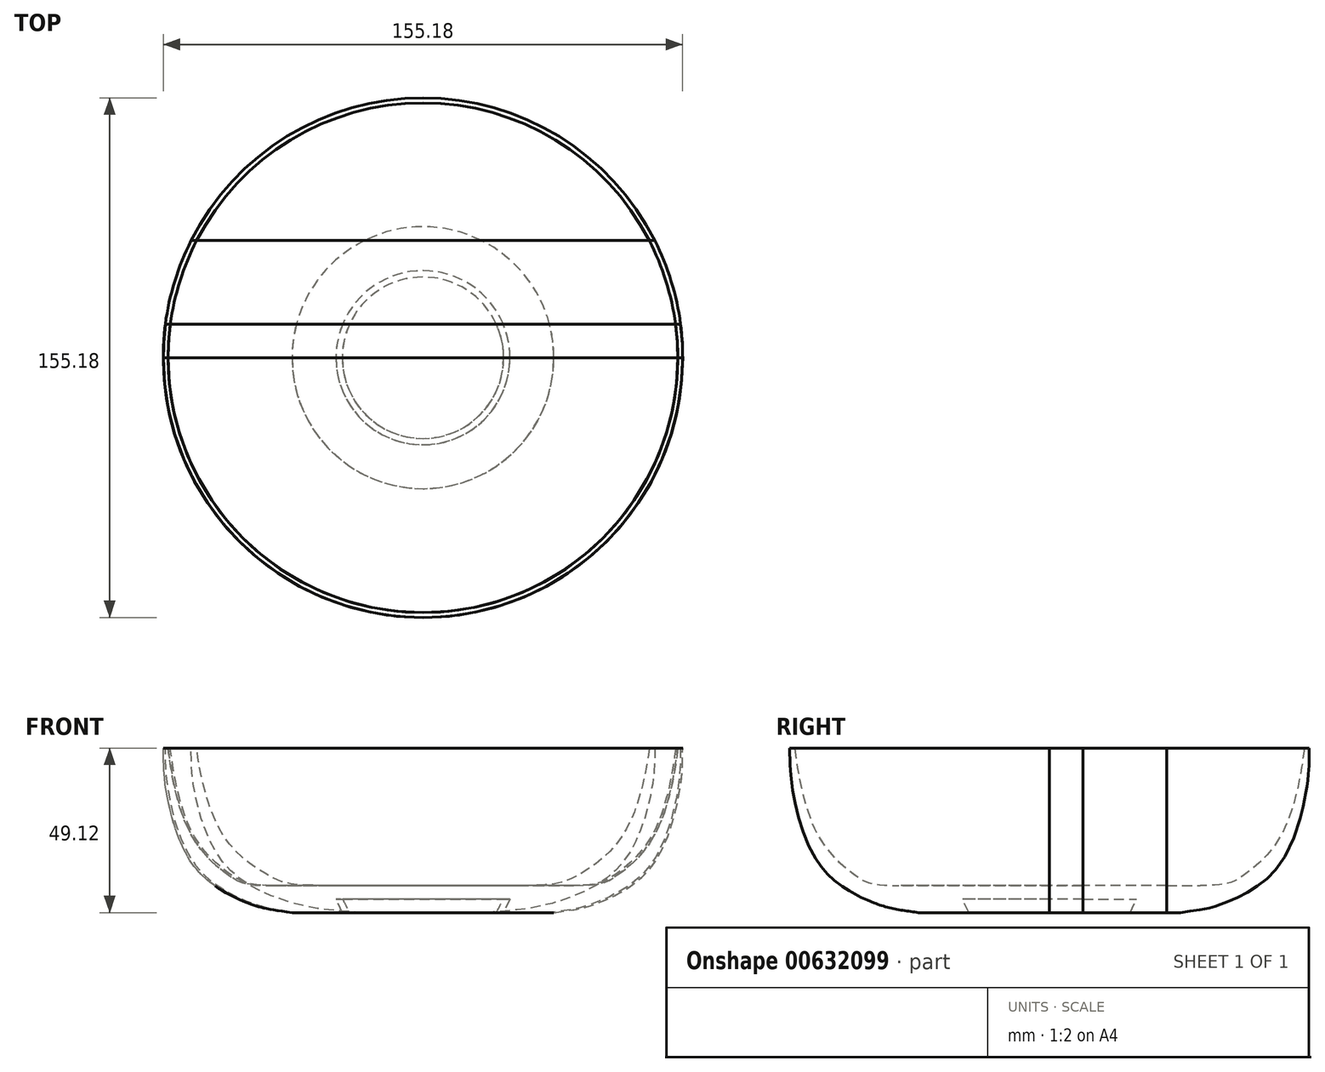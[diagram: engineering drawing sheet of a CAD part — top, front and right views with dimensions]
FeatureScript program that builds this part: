
annotation { "Feature Type Name" : "Feature", "Feature Type Description" : "" }
export const myFeature = defineFeature(function(context is Context, id is Id, definition is map)
    precondition{}
    {
        {
            var Q0;
            Q0=qCreatedBy(makeId("Top.planeOp"),FACE);
            var sketch = newSketch(context, id + "F0", { "sketchPlane" : qUnion([Q0])});
            skLineSegment(sketch, "E0.bottom", {"start": v(0, 0) * mm, "end": v(90, 0) * mm});
            skLineSegment(sketch, "E0.top", {"start": v(0, 25) * mm, "end": v(90, 25) * mm});
            skLineSegment(sketch, "E0.left", {"start": v(0, 0) * mm, "end": v(0, 25) * mm});
            skLineSegment(sketch, "E1.bottom", {"start": v(90, 25) * mm, "end": v(115, 25) * mm});
            skLineSegment(sketch, "E1.top", {"start": v(100, 0) * mm, "end": v(115, 0) * mm});
            skLineSegment(sketch, "E2.bottom", {"start": v(115, 25) * mm, "end": v(160, 25) * mm});
            skLineSegment(sketch, "E2.top", {"start": v(125, 0) * mm, "end": v(160, 0) * mm});
            skLineSegment(sketch, "E2.right", {"start": v(160, 25) * mm, "end": v(160, 0) * mm});
            skLineSegment(sketch, "E3.top", {"start": v(0, 70) * mm, "end": v(90, 70) * mm});
            skLineSegment(sketch, "E3.left", {"start": v(0, 25) * mm, "end": v(0, 70) * mm});
            skLineSegment(sketch, "E4.bottom", {"start": v(90, 70) * mm, "end": v(115, 70) * mm});
            skLineSegment(sketch, "E5.bottom", {"start": v(115, 70) * mm, "end": v(160, 70) * mm});
            skLineSegment(sketch, "E5.right", {"start": v(160, 70) * mm, "end": v(160, 25) * mm});
            skLineSegment(sketch, "E6.top", {"start": v(0, -90) * mm, "end": v(90, -90) * mm});
            skLineSegment(sketch, "E6.left", {"start": v(0, 0) * mm, "end": v(0, -90) * mm});
            skLineSegment(sketch, "E7.bottom", {"start": v(90, 0) * mm, "end": v(115, 0) * mm});
            skLineSegment(sketch, "E7.top", {"start": v(90, -90) * mm, "end": v(115, -90) * mm});
            skLineSegment(sketch, "E8.bottom", {"start": v(115, 0) * mm, "end": v(160, 0) * mm});
            skLineSegment(sketch, "E8.top", {"start": v(115, -90) * mm, "end": v(160, -90) * mm});
            skLineSegment(sketch, "E8.right", {"start": v(160, 0) * mm, "end": v(160, -90) * mm});
            skLineSegment(sketch, "E9", {"start": v(0, -10) * mm, "end": v(160, -10) * mm});
            skLineSegment(sketch, "E10", {"start": v(80, -99.76) * mm, "end": v(80, 101.9) * mm, "construction": true});
            skSolve(sketch);
        }
        {
            var Q0;
            Q0=makeQuery(id+"F0.imprint","IMPRINT",FACE,{"disambiguationData":[TD([[makeQuery(id+"F0.imprint","IMPRINT",EDGE,{"derivedFrom":sQuery(id+"F0.wireOp",EDGE,"E0.top")}),1.0]])]});
            extrude(context, id + "F1", {"entities" : qUnion([Q0]), "depth" : 50 * mm, "offsetDistance" : 25 * mm});
        }
        {
            var Q0;
            Q0=makeQuery(id+"F0.imprint","IMPRINT",FACE,{"disambiguationData":[TD([[makeQuery(id+"F0.imprint","IMPRINT",EDGE,{"derivedFrom":sQuery(id+"F0.wireOp",EDGE,"E4.bottom")}),-1.0]])]});
            extrude(context, id + "F2", {"entities" : qUnion([Q0]), "depth" : 50 * mm, "offsetDistance" : 25 * mm});
        }
        {
            var Q0;
            Q0=makeQuery(id+"F0.imprint","IMPRINT",FACE,{"disambiguationData":[TD([[makeQuery(id+"F0.imprint","IMPRINT",EDGE,{"derivedFrom":sQuery(id+"F0.wireOp",EDGE,"E5.bottom")}),-1.0]])]});
            extrude(context, id + "F3", {"entities" : qUnion([Q0]), "depth" : 50 * mm, "offsetDistance" : 25 * mm});
        }
        {
            var Q0;
            Q0=makeQuery(id+"F0.imprint","IMPRINT",FACE,{"disambiguationData":[TD([[makeQuery(id+"F0.imprint","IMPRINT",EDGE,{"derivedFrom":sQuery(id+"F0.wireOp",EDGE,"E0.left")}),-1.0]])]});
            extrude(context, id + "F4", {"entities" : qUnion([Q0]), "depth" : 50 * mm, "offsetDistance" : 25 * mm});
        }
        {
            var Q0;
            Q0=makeQuery(id+"F0.imprint","IMPRINT",FACE,{"disambiguationData":[TD([[makeQuery(id+"F0.imprint","IMPRINT",EDGE,{"derivedFrom":sQuery(id+"F0.wireOp",EDGE,"E1.left")}),1.0]])]});
            var Q1;
            {var subQ0=sQuery(id+"F0.wireOp",EDGE,"E0.bottom");Q1=makeQuery(id+"F0.imprint","IMPRINT",FACE,{"disambiguationData":[TD([[makeQuery(id+"F0.imprint","IMPRINT",EDGE,{"derivedFrom":subQ0}),-1.0]])]});}
            var Q2;
            {var subQ0=sQuery(id+"F0.wireOp",EDGE,"E8.bottom");Q2=makeQuery(id+"F0.imprint","IMPRINT",FACE,{"disambiguationData":[TD([[makeQuery(id+"F0.imprint","IMPRINT",EDGE,{"derivedFrom":subQ0}),-1.0]])]});}
            var Q3;
            {var subQ0=sQuery(id+"F0.wireOp",EDGE,"E6.top");Q3=makeQuery(id+"F0.imprint","IMPRINT",FACE,{"disambiguationData":[TD([[makeQuery(id+"F0.imprint","IMPRINT",EDGE,{"derivedFrom":subQ0}),1.0]])]});}
            var Q4;
            {var subQ0=sQuery(id+"F0.wireOp",EDGE,"E8.top");Q4=makeQuery(id+"F0.imprint","IMPRINT",FACE,{"disambiguationData":[TD([[makeQuery(id+"F0.imprint","IMPRINT",EDGE,{"derivedFrom":subQ0}),1.0]])]});}
            extrude(context, id + "F5", {"entities" : qUnion([Q0, Q1, Q2, Q3, Q4]), "depth" : 50 * mm, "offsetDistance" : 25 * mm});
        }
        {
            var Q0;
            {var subQ0=sQuery(id+"F0.wireOp",EDGE,"E7.bottom");Q0=makeQuery(id+"F0.imprint","IMPRINT",FACE,{"disambiguationData":[TD([[makeQuery(id+"F0.imprint","IMPRINT",EDGE,{"derivedFrom":subQ0}),-1.0]])]});}
            var Q1;
            {var subQ0=sQuery(id+"F0.wireOp",EDGE,"E7.top");Q1=makeQuery(id+"F0.imprint","IMPRINT",FACE,{"disambiguationData":[TD([[makeQuery(id+"F0.imprint","IMPRINT",EDGE,{"derivedFrom":subQ0}),1.0]])]});}
            extrude(context, id + "F6", {"entities" : qUnion([Q0, Q1]), "depth" : 50 * mm, "offsetDistance" : 25 * mm});
        }
        {
            var Q0;
            {var subQ0=sQuery(id+"F0.wireOp",EDGE,"E0.bottom");Q0=makeQuery(id+"F0.imprint","IMPRINT",FACE,{"disambiguationData":[TD([[makeQuery(id+"F0.imprint","IMPRINT",EDGE,{"derivedFrom":subQ0}),-1.0]])]});}
            extrude(context, id + "F7", {"entities" : qUnion([Q0]), "depth" : 50 * mm, "offsetDistance" : 25 * mm});
        }
        {
            var Q0;
            {var subQ0=sQuery(id+"F0.wireOp",EDGE,"E7.bottom");Q0=makeQuery(id+"F0.imprint","IMPRINT",FACE,{"disambiguationData":[TD([[makeQuery(id+"F0.imprint","IMPRINT",EDGE,{"derivedFrom":subQ0}),-1.0]])]});}
            extrude(context, id + "F8", {"entities" : qUnion([Q0]), "depth" : 50 * mm, "offsetDistance" : 25 * mm});
        }
        {
            var Q0;
            {var subQ0=sQuery(id+"F0.wireOp",EDGE,"E8.bottom");Q0=makeQuery(id+"F0.imprint","IMPRINT",FACE,{"disambiguationData":[TD([[makeQuery(id+"F0.imprint","IMPRINT",EDGE,{"derivedFrom":subQ0}),-1.0]])]});}
            extrude(context, id + "F9", {"entities" : qUnion([Q0]), "depth" : 50 * mm, "offsetDistance" : 25 * mm});
        }
        {
            var Q0;
            {var subQ0=sQuery(id+"F0.wireOp",EDGE,"E6.top");Q0=makeQuery(id+"F0.imprint","IMPRINT",FACE,{"disambiguationData":[TD([[makeQuery(id+"F0.imprint","IMPRINT",EDGE,{"derivedFrom":subQ0}),1.0]])]});}
            extrude(context, id + "F10", {"entities" : qUnion([Q0]), "depth" : 50 * mm, "offsetDistance" : 25 * mm});
        }
        {
            var Q0;
            {var subQ0=sQuery(id+"F0.wireOp",EDGE,"E7.top");Q0=makeQuery(id+"F0.imprint","IMPRINT",FACE,{"disambiguationData":[TD([[makeQuery(id+"F0.imprint","IMPRINT",EDGE,{"derivedFrom":subQ0}),1.0]])]});}
            extrude(context, id + "F11", {"entities" : qUnion([Q0]), "depth" : 50 * mm, "offsetDistance" : 25 * mm});
        }
        {
            var Q0;
            {var subQ0=sQuery(id+"F0.wireOp",EDGE,"E8.top");Q0=makeQuery(id+"F0.imprint","IMPRINT",FACE,{"disambiguationData":[TD([[makeQuery(id+"F0.imprint","IMPRINT",EDGE,{"derivedFrom":subQ0}),1.0]])]});}
            extrude(context, id + "F12", {"entities" : qUnion([Q0]), "depth" : 50 * mm, "offsetDistance" : 25 * mm});
        }
        {
            var Q0;
            Q0=makeQuery(id+"F7.opExtrude","SWEPT_FACE",FACE,{"disambiguationData":[OSD([sQuery(id+"F0.wireOp",EDGE,"E9")])]});
            var sketch = newSketch(context, id + "F13", { "sketchPlane" : qUnion([Q0])});
            skLineSegment(sketch, "E11", {"start": v(80, 72.12) * mm, "end": v(80, -27.18) * mm, "construction": true});
            skLineSegment(sketch, "E12", {"start": v(80, 4) * mm, "end": v(106, 4) * mm});
            skLineSegment(sketch, "E13", {"start": v(106, 4) * mm, "end": v(104.1, 0) * mm});
            skLineSegment(sketch, "E14", {"start": v(104.1, 0) * mm, "end": v(119.1, 0) * mm});
            skLineSegment(sketch, "E15", {"start": v(80, 8.1) * mm, "end": v(125, 8.1) * mm});
            skFitSpline(sketch, "E16", {"points": [v(125, 8.1) * mm, v(137.42, 10.74) * mm, v(148.74, 22.34) * mm, v(156.11, 49) * mm], "startDerivative": vector(87.08, 0) * mm, "endDerivative": vector(7.06, 60.03) * mm});
            skLineSegment(sketch, "E17", {"start": v(156.11, 49) * mm, "end": v(157.6, 49.12) * mm});
            skLineSegment(sketch, "E18", {"start": v(80, 8.1) * mm, "end": v(80, 4) * mm});
            skFitSpline(sketch, "E19", {"points": [v(119.1, 0) * mm, v(132.7, 3.03) * mm, v(148.24, 13.65) * mm, v(156.75, 36.8) * mm, v(157.6, 49.12) * mm], "startDerivative": vector(102.12, 13.3) * mm, "endDerivative": vector(0.04, 70.37) * mm});
            skSolve(sketch);
        }
        {
            var Q0;
            {var subQ0=sQuery(id+"F13.wireOp",EDGE,"E18");Q0=makeQuery(id+"F13.imprint","IMPRINT",FACE,{"disambiguationData":[TD([[makeQuery(id+"F13.imprint","IMPRINT",EDGE,{"derivedFrom":subQ0}),1.0]])]});}
            var Q1;
            {var subQ3=sQuery(id+"F13.wireOp",EDGE,"f76ab763-0c6e-4cc8-a736-abfbcbe2b951");Q1=makeQuery(id+"F13.imprint","IMPRINT",FACE,{"disambiguationData":[TD([[makeQuery(id+"F13.imprint","IMPRINT",EDGE,{"derivedFrom":subQ3}),1.0]])]});}
            var Q2;
            {var subQ0=sQuery(id+"F13.wireOp",EDGE,"E14");var subQ1=sQuery(id+"F13.wireOp",EDGE,"E13");var subQ2=sQuery(id+"F0.wireOp",EDGE,"E9");var subQ3=makeQuery(id+"F13.imprint","INTERSECT",VERTEX,{"derivedFrom":[makeQuery(id+"F7.opExtrude","CAP_EDGE",EDGE,{"disambiguationData":[OSD([subQ2])],"isStart":true}),subQ1,subQ0]});Q2=makeQuery(id+"F13.imprint","IMPRINT",FACE,{"disambiguationData":[TD([[makeQuery(id+"F13.imprint","IMPRINT",EDGE,{"disambiguationData":[TD([[subQ3,1.0]])],"derivedFrom":subQ1}),1.0]])]});}
            var Q3;
            Q3=sQuery(id+"F13.wireOp",EDGE,"E11");
            revolve(context, id + "F14", {"operationType" : NewBodyOperationType.INTERSECT, "entities" : qUnion([Q0, Q1, Q2]), "axis" : qUnion([Q3]), "revolveType" : RevolveType.FULL, "oppositeDirection" : true});
        }
    });
